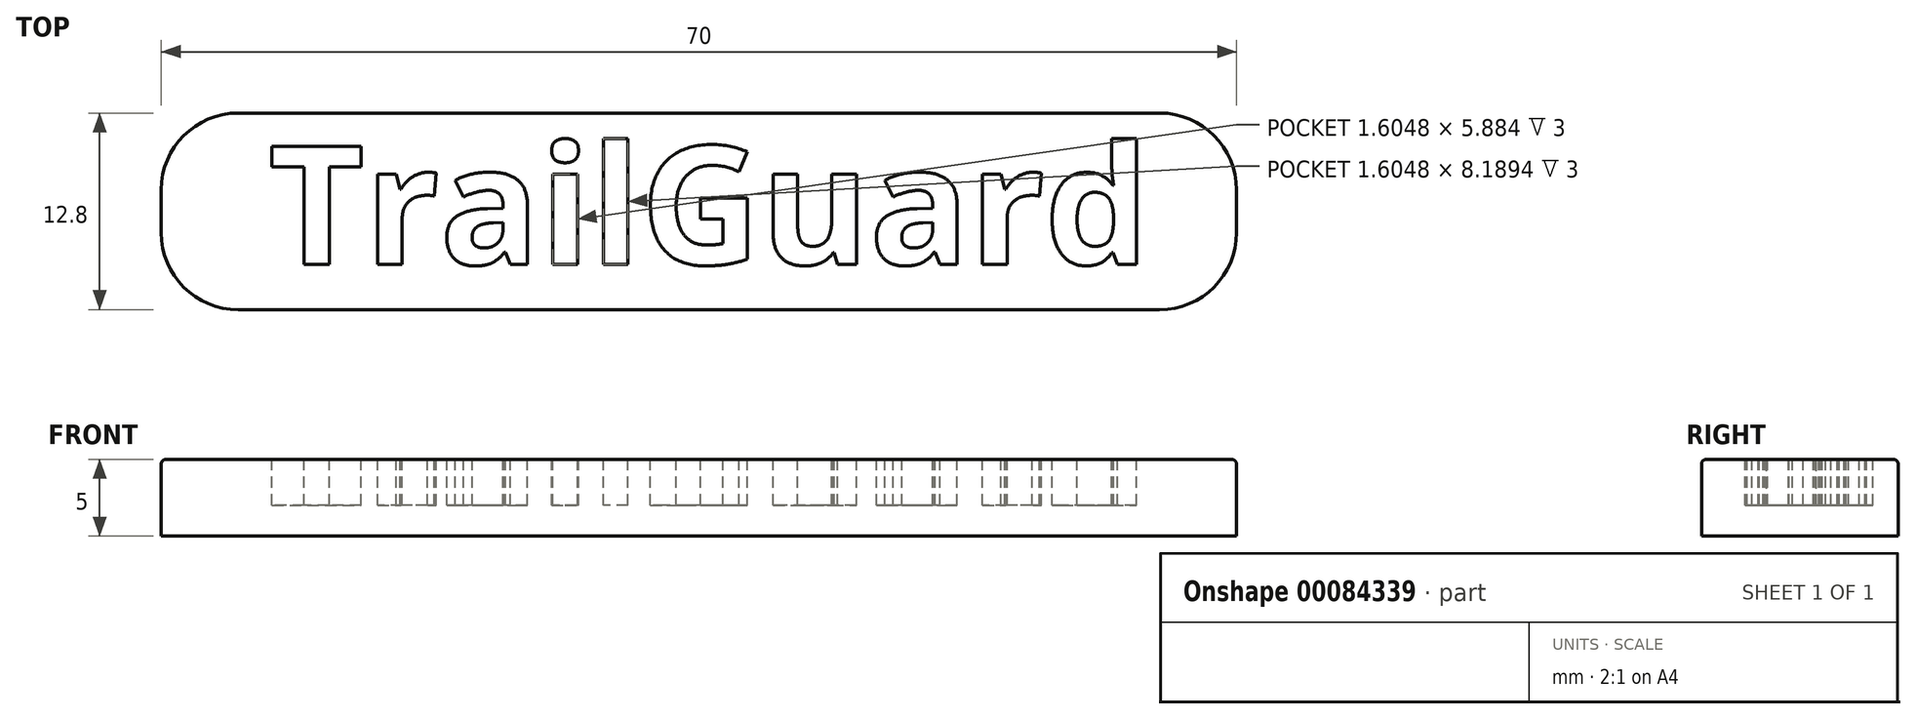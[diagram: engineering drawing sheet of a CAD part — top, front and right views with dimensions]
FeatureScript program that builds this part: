
annotation { "Feature Type Name" : "Feature", "Feature Type Description" : "" }
export const myFeature = defineFeature(function(context is Context, id is Id, definition is map)
    precondition{}
    {
        {
            var Q0;
            Q0=qCreatedBy(makeId("Top.planeOp"),FACE);
            var sketch = newSketch(context, id + "F0", { "sketchPlane" : qUnion([Q0])});
            skLineSegment(sketch, "E0.bottom", {"start": v(30, 6.4) * mm, "end": v(-30, 6.4) * mm});
            skLineSegment(sketch, "E0.top", {"start": v(30, -6.4) * mm, "end": v(-30, -6.4) * mm});
            skLineSegment(sketch, "E0.left", {"start": v(35, 1.4) * mm, "end": v(35, -1.4) * mm});
            skLineSegment(sketch, "E0.right", {"start": v(-35, 1.4) * mm, "end": v(-35, -1.4) * mm});
            skPoint(sketch, "E0.middle", {"position": v(0, 0) * mm});
            skPoint(sketch, "E1.visualSharp", {"position": v(-35, 6.4) * mm});
            skArc(sketch, "E1.filletArc", {"start": v(-30, 6.4) * mm, "mid": v(-33.54, 4.94) * mm, "end": v(-35, 1.4) * mm});
            skPoint(sketch, "E2.visualSharp", {"position": v(-35, -6.4) * mm});
            skArc(sketch, "E2.filletArc", {"start": v(-35, -1.4) * mm, "mid": v(-33.54, -4.94) * mm, "end": v(-30, -6.4) * mm});
            skPoint(sketch, "E3.visualSharp", {"position": v(35, 6.4) * mm});
            skArc(sketch, "E3.filletArc", {"start": v(35, 1.4) * mm, "mid": v(33.54, 4.94) * mm, "end": v(30, 6.4) * mm});
            skPoint(sketch, "E4.visualSharp", {"position": v(35, -6.4) * mm});
            skArc(sketch, "E4.filletArc", {"start": v(30, -6.4) * mm, "mid": v(33.54, -4.94) * mm, "end": v(35, -1.4) * mm});
            skSolve(sketch);
        }
        {
            var Q0;
            Q0=makeQuery(id+"F0.imprint","IMPRINT",FACE,{"disambiguationData":[TD([[makeQuery(id+"F0.imprint","IMPRINT",EDGE,{"derivedFrom":sQuery(id+"F0.wireOp",EDGE,"E0.bottom")}),1.0]])]});
            extrude(context, id + "F1", {"entities" : qUnion([Q0]), "oppositeDirection" : true, "depth" : 5 * mm});
        }
        {
            var Q0;
            Q0=makeQuery(id+"F1.opExtrude","CAP_FACE",FACE,{"disambiguationData":[OSD([sQuery(id+"F0.wireOp",EDGE,"E0.bottom"),sQuery(id+"F0.wireOp",EDGE,"E0.top"),sQuery(id+"F0.wireOp",EDGE,"E0.left"),sQuery(id+"F0.wireOp",EDGE,"E0.right"),sQuery(id+"F0.wireOp",EDGE,"E1.filletArc"),sQuery(id+"F0.wireOp",EDGE,"E2.filletArc"),sQuery(id+"F0.wireOp",EDGE,"E3.filletArc"),sQuery(id+"F0.wireOp",EDGE,"E4.filletArc")])],"isStart":true});
            var sketch = newSketch(context, id + "F2", { "sketchPlane" : qUnion([Q0])});
            skText(sketch, "E5", { "text": "TrailGuard", "fontName": "OpenSans-Bold.ttf"});
            const initialGuessF2  = {"E5": [-0.028, -0.00345, 1, 0, 0.00776]};
            skSetInitialGuess(sketch, initialGuessF2);
            skSolve(sketch);
        }
        {
            var Q0;
            Q0 = qSketchRegion(id + "F2", true);
            extrude(context, id + "F3", {"entities" : qUnion([Q0]), "operationType" : NewBodyOperationType.REMOVE, "oppositeDirection" : true, "depth" : 3 * mm});
        }
        {
            var Q0;
            Q0=makeQuery(id+"F1.opExtrude","CAP_EDGE",EDGE,{"disambiguationData":[OSD([sQuery(id+"F0.wireOp",EDGE,"E0.bottom")])],"isStart":true});
            var Q1;
            Q1=makeQuery(id+"F1.opExtrude","CAP_EDGE",EDGE,{"disambiguationData":[OSD([sQuery(id+"F0.wireOp",EDGE,"E0.top")])],"isStart":true});
            var Q2;
            Q2=makeQuery(id+"F1.opExtrude","CAP_EDGE",EDGE,{"disambiguationData":[OSD([sQuery(id+"F0.wireOp",EDGE,"E4.filletArc")])],"isStart":true});
            var Q3;
            Q3=makeQuery(id+"F1.opExtrude","CAP_EDGE",EDGE,{"disambiguationData":[OSD([sQuery(id+"F0.wireOp",EDGE,"E0.left")])],"isStart":true});
            var Q4;
            Q4=makeQuery(id+"F1.opExtrude","CAP_EDGE",EDGE,{"disambiguationData":[OSD([sQuery(id+"F0.wireOp",EDGE,"E3.filletArc")])],"isStart":true});
            var Q5;
            Q5=makeQuery(id+"F1.opExtrude","CAP_EDGE",EDGE,{"disambiguationData":[OSD([sQuery(id+"F0.wireOp",EDGE,"E1.filletArc")])],"isStart":true});
            var Q6;
            Q6=makeQuery(id+"F1.opExtrude","CAP_EDGE",EDGE,{"disambiguationData":[OSD([sQuery(id+"F0.wireOp",EDGE,"E0.right")])],"isStart":true});
            var Q7;
            Q7=makeQuery(id+"F1.opExtrude","CAP_EDGE",EDGE,{"disambiguationData":[OSD([sQuery(id+"F0.wireOp",EDGE,"E2.filletArc")])],"isStart":true});
            fillet(context, id + "F4", {"entities" : qUnion([Q0, Q1, Q2, Q3, Q4, Q5, Q6, Q7]), "radius" : .3 * mm, "tangentPropagation" : true, "allowEdgeOverflow" : false});
        }
    });
